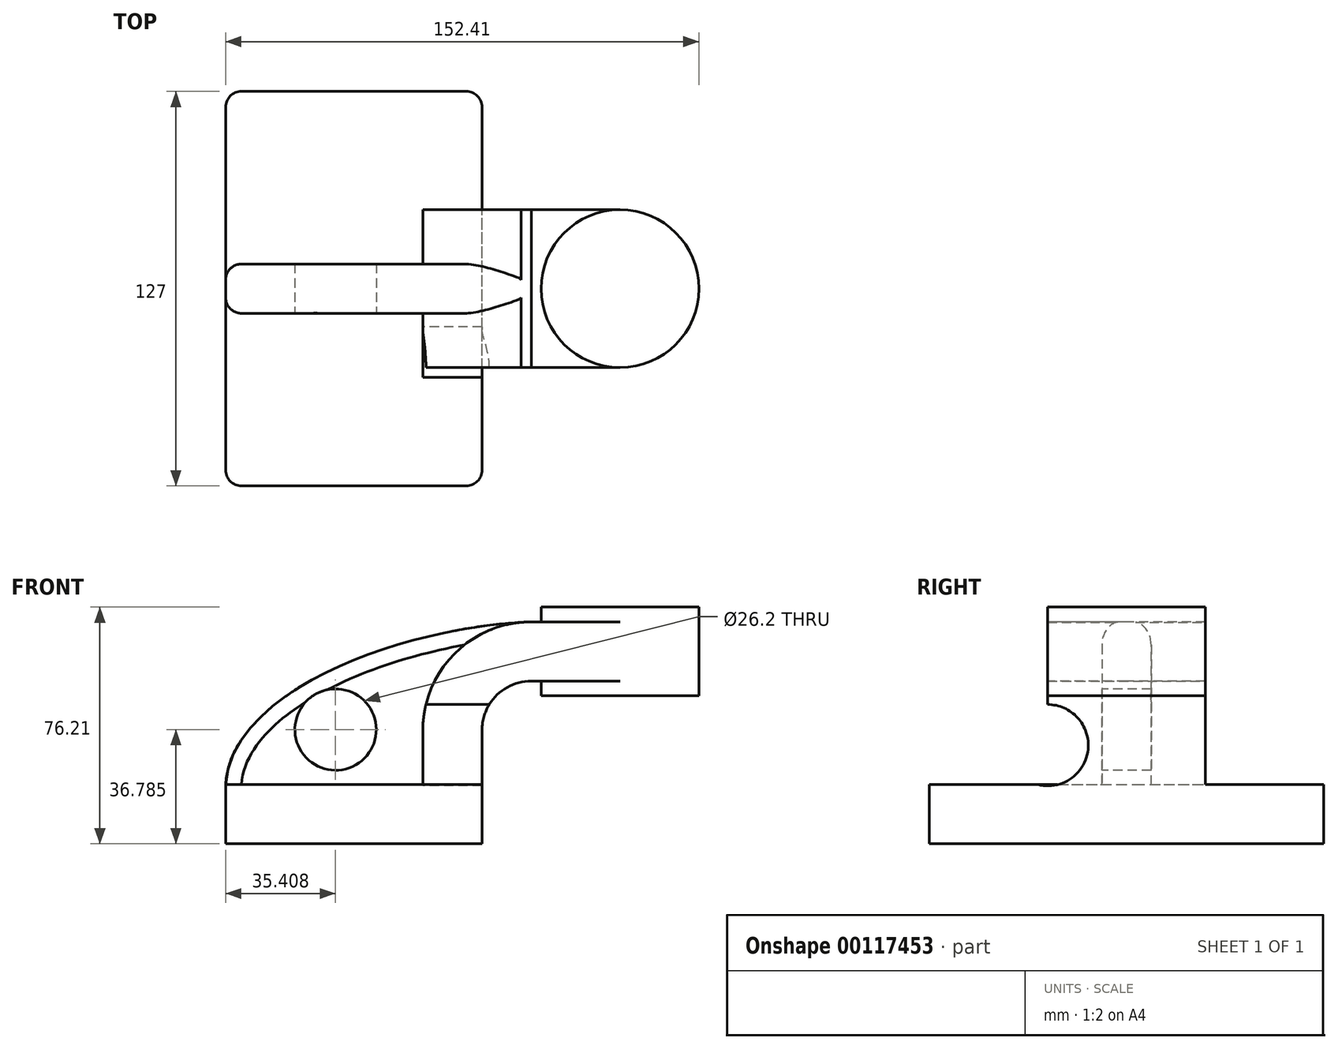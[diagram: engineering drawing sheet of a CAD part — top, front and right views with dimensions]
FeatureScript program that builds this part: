
annotation { "Feature Type Name" : "Feature", "Feature Type Description" : "" }
export const myFeature = defineFeature(function(context is Context, id is Id, definition is map)
    precondition{}
    {
        {
            var Q0;
            Q0=qCreatedBy(makeId("Front.planeOp"),FACE);
            var sketch = newSketch(context, id + "F0", { "sketchPlane" : qUnion([Q0])});
            skLineSegment(sketch, "E0.rect.bottom", {"start": v(-41.28, 9.52) * mm, "end": v(41.28, 9.52) * mm});
            skLineSegment(sketch, "E0.rect.top", {"start": v(-41.28, -9.52) * mm, "end": v(41.28, -9.52) * mm});
            skLineSegment(sketch, "E0.rect.left", {"start": v(-41.28, 9.52) * mm, "end": v(-41.28, -9.52) * mm});
            skLineSegment(sketch, "E0.rect.right", {"start": v(41.28, 9.52) * mm, "end": v(41.28, -9.52) * mm});
            skPoint(sketch, "E0.rect.middle", {"position": v(0, 0) * mm});
            skLineSegment(sketch, "E1", {"start": v(41.28, 9.52) * mm, "end": v(41.28, 27) * mm});
            skArc(sketch, "E2", {"start": v(41.28, 27) * mm, "mid": v(45.92, 38.23) * mm, "end": v(57.15, 42.88) * mm});
            skLineSegment(sketch, "E3", {"start": v(57.15, 42.88) * mm, "end": v(85.72, 42.88) * mm});
            skLineSegment(sketch, "E4.rect.bottom", {"start": v(60.32, 38.1) * mm, "end": v(111.12, 38.1) * mm});
            skLineSegment(sketch, "E4.rect.top", {"start": v(60.32, 66.68) * mm, "end": v(111.12, 66.68) * mm});
            skLineSegment(sketch, "E4.rect.left", {"start": v(60.32, 38.1) * mm, "end": v(60.32, 66.68) * mm});
            skLineSegment(sketch, "E4.rect.right", {"start": v(111.13, 38.1) * mm, "end": v(111.12, 66.68) * mm});
            skPoint(sketch, "E4.rect.middle", {"position": v(85.72, 52.39) * mm});
            skLineSegment(sketch, "E5.0", {"start": v(57.15, 61.93) * mm, "end": v(85.72, 61.93) * mm});
            skArc(sketch, "E5.1", {"start": v(22.23, 27) * mm, "mid": v(32.45, 51.7) * mm, "end": v(57.15, 61.93) * mm});
            skLineSegment(sketch, "E5.2", {"start": v(22.23, 9.52) * mm, "end": v(22.23, 27) * mm});
            skLineSegment(sketch, "E6", {"start": v(85.72, 38.1) * mm, "end": v(85.72, 66.68) * mm});
            skFitSpline(sketch, "E7", {"points": [v(-41.28, 9.53) * mm, v(57.15, 61.93) * mm], "startDerivative": vector(5.2, 92.34) * mm, "endDerivative": vector(120.92, 4.22) * mm});
            skSolve(sketch);
        }
        {
            var Q0;
            Q0=makeQuery(id+"F0.imprint","IMPRINT",FACE,{"disambiguationData":[TD([[makeQuery(id+"F0.imprint","IMPRINT",EDGE,{"derivedFrom":sQuery(id+"F0.wireOp",EDGE,"E0.rect.top")}),1.0]])]});
            extrude(context, id + "F1", {"entities" : qUnion([Q0]), "endBound" : BoundingType.SYMMETRIC, "depth" : 127 * mm});
        }
        {
            var Q0;
            {var subQ9=sQuery(id+"F0.wireOp",EDGE,"E1");Q0=makeQuery(id+"F0.imprint","IMPRINT",FACE,{"disambiguationData":[TD([[makeQuery(id+"F0.imprint","IMPRINT",EDGE,{"derivedFrom":subQ9}),1.0]])]});}
            var Q1;
            {var subQ0=sQuery(id+"F0.wireOp",EDGE,"E6");var subQ1=sQuery(id+"F0.wireOp",EDGE,"E3");var subQ2=makeQuery(id+"F0.imprint","INTERSECT",VERTEX,{"derivedFrom":[subQ1,subQ0]});Q1=makeQuery(id+"F0.imprint","IMPRINT",FACE,{"disambiguationData":[TD([[makeQuery(id+"F0.imprint","IMPRINT",EDGE,{"disambiguationData":[TD([[subQ2,1.0]])],"derivedFrom":subQ1}),1.0]])]});}
            extrude(context, id + "F2", {"entities" : qUnion([Q0, Q1]), "operationType" : NewBodyOperationType.ADD, "endBound" : BoundingType.SYMMETRIC, "depth" : 50.8 * mm});
        }
        {
            var Q0;
            {var subQ3=sQuery(id+"F0.wireOp",EDGE,"E5.2");Q0=makeQuery(id+"F0.imprint","IMPRINT",FACE,{"disambiguationData":[TD([[makeQuery(id+"F0.imprint","IMPRINT",EDGE,{"derivedFrom":subQ3}),1.0]])]});}
            extrude(context, id + "F3", {"entities" : qUnion([Q0]), "operationType" : NewBodyOperationType.ADD, "endBound" : BoundingType.SYMMETRIC, "depth" : 15.88 * mm});
        }
        {
            var Q0;
            {var subQ5=sQuery(id+"F0.wireOp",EDGE,"E4.rect.right");Q0=makeQuery(id+"F0.imprint","IMPRINT",FACE,{"disambiguationData":[TD([[makeQuery(id+"F0.imprint","IMPRINT",EDGE,{"derivedFrom":subQ5}),1.0]])]});}
            var Q1;
            Q1=sQuery(id+"F0.wireOp",EDGE,"E6");
            revolve(context, id + "F4", {"operationType" : NewBodyOperationType.ADD, "entities" : qUnion([Q0]), "axis" : qUnion([Q1]), "revolveType" : RevolveType.FULL});
        }
        {
            var Q0;
            Q0=makeQuery(id+"F1.opExtrude","CAP_EDGE",EDGE,{"disambiguationData":[OSD([sQuery(id+"F0.wireOp",EDGE,"E0.rect.right")])],"isStart":false});
            var Q1;
            Q1=makeQuery(id+"F1.opExtrude","CAP_EDGE",EDGE,{"disambiguationData":[OSD([sQuery(id+"F0.wireOp",EDGE,"E0.rect.left")])],"isStart":false});
            var Q2;
            Q2=makeQuery(id+"F1.opExtrude","CAP_EDGE",EDGE,{"disambiguationData":[OSD([sQuery(id+"F0.wireOp",EDGE,"E0.rect.right")])],"isStart":true});
            var Q3;
            Q3=makeQuery(id+"F1.opExtrude","CAP_EDGE",EDGE,{"disambiguationData":[OSD([sQuery(id+"F0.wireOp",EDGE,"E0.rect.left")])],"isStart":true});
            fillet(context, id + "F5", {"entities" : qUnion([Q0, Q1, Q2, Q3]), "radius" : 5.08 * mm, "tangentPropagation" : true, "allowEdgeOverflow" : false});
        }
        {
            var Q0;
            {var subQ0=sQuery(id+"F0.wireOp",EDGE,"E0.rect.bottom");var subQ1=sQuery(id+"F0.wireOp",EDGE,"E7");var subQ2=sQuery(id+"F0.wireOp",EDGE,"E5.2");var subQ3=sQuery(id+"F0.wireOp",EDGE,"E5.1");Q0=makeQuery(id+"F3.boolean.opBoolean","SPLIT",FACE,{"disambiguationData":[TD([makeQuery(id+"F3.opExtrude","CAP_FACE",FACE,{"disambiguationData":[OSD([subQ0,subQ3,subQ2,subQ1])],"isStart":false})])],"derivedFrom":makeQuery(id+"F2.opExtrude","SWEPT_FACE",FACE,{"disambiguationData":[OSD([subQ2])]})});}
            var sketch = newSketch(context, id + "F6", { "sketchPlane" : qUnion([Q0])});
            skCircle(sketch, "E8", {"center": v(25.4, 22.22) * mm, "radius": 2.54 * mm});
            skSolve(sketch);
        }
        {
            var Q0;
            Q0=makeQuery(id+"F3.opExtrude","CAP_FACE",FACE,{"disambiguationData":[OSD([sQuery(id+"F0.wireOp",EDGE,"E0.rect.bottom"),sQuery(id+"F0.wireOp",EDGE,"E5.1"),sQuery(id+"F0.wireOp",EDGE,"E5.2"),sQuery(id+"F0.wireOp",EDGE,"E7")])],"isStart":false});
            var sketch = newSketch(context, id + "F7", { "sketchPlane" : qUnion([Q0])});
            skCircle(sketch, "E9", {"center": v(-5.87, 27.25) * mm, "radius": 13.35 * mm});
            skSolve(sketch);
        }
        {
            var Q0;
            Q0=sQuery(id+"F7.wireOp",VERTEX,"E9.center");
            var Q1;
            Q1=sQuery(id+"F6.wireOp",VERTEX,"E8.center");
            var Q2;
            Q2=makeQuery(id+"F1.opExtrude","SWEPT_BODY",BODY,{"disambiguationData":[OSD([sQuery(id+"F0.wireOp",EDGE,"E0.rect.bottom"),sQuery(id+"F0.wireOp",EDGE,"E0.rect.top"),sQuery(id+"F0.wireOp",EDGE,"E0.rect.left"),sQuery(id+"F0.wireOp",EDGE,"E0.rect.right")])]});
            hole(context, id + "F8", {"style" : HoleStyle.SIMPLE, "endStyle" : HoleEndStyle.THROUGH, "standardTappedOrClearance" : lookupTablePath({ "standard" : "ANSI", "fit" : "Normal (ASME)", "size" : "1", "type" : "Clearance" }), "standardBlindInLast" : lookupTablePath({ "fit" : "Free", "standard" : "ANSI", "size" : "1", "type" : "Clearance" }), "holeDiameter" : 26.2 * mm, "startFromSketch" : true, "locations" : qUnion([Q0, Q1]), "scope" : qUnion([Q2]), "isTappedThrough" : true});
        }
        {
            var Q0;
            Q0=makeQuery(id+"F8.hole-1.boolean.opBoolean","INTERSECT",EDGE,{"derivedFrom":[makeQuery(id+"F2.opExtrude","CAP_FACE",FACE,{"disambiguationData":[OSD([sQuery(id+"F0.wireOp",EDGE,"E0.rect.bottom"),sQuery(id+"F0.wireOp",EDGE,"E1"),sQuery(id+"F0.wireOp",EDGE,"E2"),sQuery(id+"F0.wireOp",EDGE,"E3"),sQuery(id+"F0.wireOp",EDGE,"E5.0"),sQuery(id+"F0.wireOp",EDGE,"E5.1"),sQuery(id+"F0.wireOp",EDGE,"E5.2"),sQuery(id+"F0.wireOp",EDGE,"E6"),sQuery(id+"F0.wireOp",EDGE,"E7")])],"isStart":false}),makeQuery(id+"F8.hole-1.opRevolve","SWEPT_FACE",FACE,{"disambiguationData":[OSD([sQuery(id+"F8.hole-1.sketch.wireOp",EDGE,"core_line_2")])]})]});
            var Q1;
            Q1=makeQuery(id+"F3.opExtrude","CAP_EDGE",EDGE,{"disambiguationData":[OSD([sQuery(id+"F0.wireOp",EDGE,"E7")])],"isStart":false});
            var Q2;
            Q2=makeQuery(id+"F3.opExtrude","CAP_EDGE",EDGE,{"disambiguationData":[OSD([sQuery(id+"F0.wireOp",EDGE,"E7")])],"isStart":true});
            fillet(context, id + "F9", {"entities" : qUnion([Q0, Q1, Q2]), "radius" : 5.08 * mm, "tangentPropagation" : true, "allowEdgeOverflow" : false});
        }
    });
